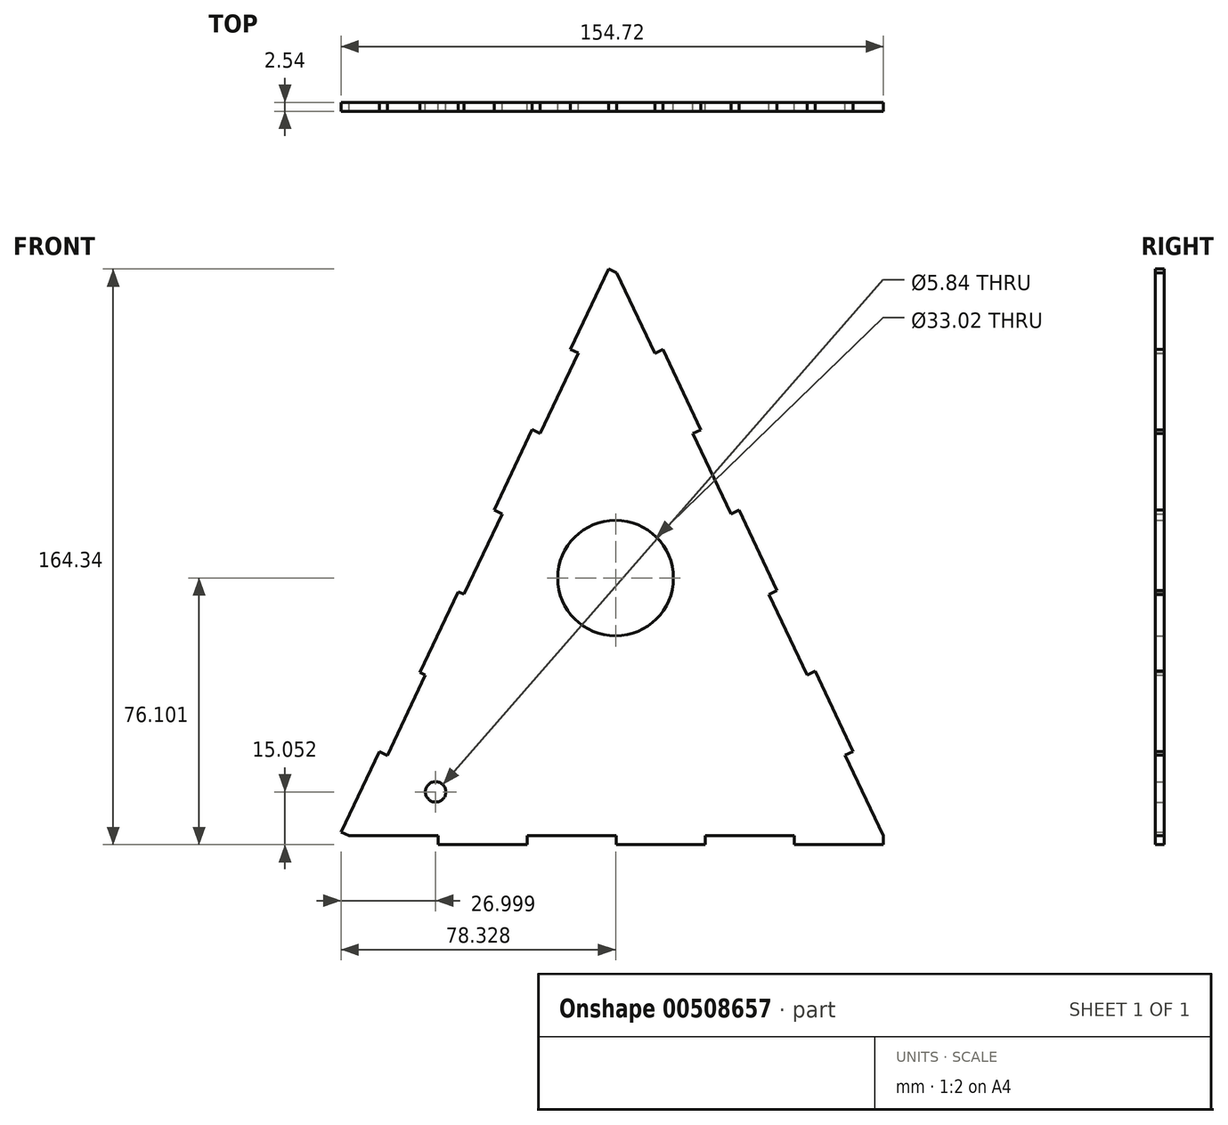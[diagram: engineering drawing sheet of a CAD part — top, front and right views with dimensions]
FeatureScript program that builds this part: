
annotation { "Feature Type Name" : "Feature", "Feature Type Description" : "" }
export const myFeature = defineFeature(function(context is Context, id is Id, definition is map)
    precondition{}
    {
        {
            var Q0;
            Q0=qCreatedBy(makeId("Front.planeOp"),FACE);
            var sketch = newSketch(context, id + "F0", { "sketchPlane" : qUnion([Q0])});
            skLineSegment(sketch, "E0", {"start": v(-10.9, 63.99) * mm, "end": v(-54.56, -27.9) * mm});
            skLineSegment(sketch, "E1", {"start": v(-76.36, -73.78) * mm, "end": v(76.06, -73.78) * mm});
            skLineSegment(sketch, "E2", {"start": v(76.06, -73.78) * mm, "end": v(0, 86.93) * mm});
            skLineSegment(sketch, "E3", {"start": v(0, 86.93) * mm, "end": v(-2.3, 88.02) * mm});
            skLineSegment(sketch, "E4", {"start": v(-2.3, 88.02) * mm, "end": v(-13.2, 65.08) * mm});
            skLineSegment(sketch, "E5", {"start": v(-13.2, 65.08) * mm, "end": v(-10.9, 63.99) * mm});
            skLineSegment(sketch, "E6", {"start": v(-24.1, 42.14) * mm, "end": v(-35, 19.2) * mm});
            skLineSegment(sketch, "E7", {"start": v(-35, 19.2) * mm, "end": v(-32.7, 18.1) * mm});
            skLineSegment(sketch, "E8", {"start": v(-43.6, -4.84) * mm, "end": v(-45.27, -4.19) * mm});
            skLineSegment(sketch, "E9", {"start": v(-45.27, -4.19) * mm, "end": v(-56.17, -27.13) * mm});
            skLineSegment(sketch, "E10", {"start": v(-56.17, -27.13) * mm, "end": v(-54.56, -27.9) * mm});
            skLineSegment(sketch, "E11", {"start": v(-54.56, -27.9) * mm, "end": v(-65.46, -50.84) * mm});
            skLineSegment(sketch, "E12", {"start": v(-65.46, -50.84) * mm, "end": v(-67.76, -49.75) * mm});
            skLineSegment(sketch, "E13", {"start": v(-67.76, -49.75) * mm, "end": v(-78.66, -72.7) * mm});
            skLineSegment(sketch, "E14", {"start": v(-78.66, -72.7) * mm, "end": v(-76.36, -73.78) * mm});
            skLineSegment(sketch, "E15", {"start": v(-76.36, -73.78) * mm, "end": v(-50.96, -73.78) * mm});
            skLineSegment(sketch, "E16", {"start": v(-50.96, -73.78) * mm, "end": v(-50.96, -76.32) * mm});
            skLineSegment(sketch, "E17", {"start": v(-50.96, -76.32) * mm, "end": v(-25.56, -76.32) * mm});
            skLineSegment(sketch, "E18", {"start": v(-25.56, -76.32) * mm, "end": v(-25.56, -73.78) * mm});
            skLineSegment(sketch, "E19", {"start": v(-25.56, -73.78) * mm, "end": v(-0.15, -73.78) * mm});
            skLineSegment(sketch, "E20", {"start": v(-0.15, -73.78) * mm, "end": v(-0.15, -76.32) * mm});
            skLineSegment(sketch, "E21", {"start": v(-0.15, -76.32) * mm, "end": v(25.25, -76.32) * mm});
            skLineSegment(sketch, "E22", {"start": v(25.25, -76.32) * mm, "end": v(25.25, -73.78) * mm});
            skLineSegment(sketch, "E23", {"start": v(25.25, -73.78) * mm, "end": v(50.65, -73.78) * mm});
            skLineSegment(sketch, "E24", {"start": v(50.65, -73.78) * mm, "end": v(50.65, -76.32) * mm});
            skLineSegment(sketch, "E25", {"start": v(50.65, -76.32) * mm, "end": v(76.05, -76.32) * mm});
            skLineSegment(sketch, "E26", {"start": v(76.05, -76.32) * mm, "end": v(76.06, -73.78) * mm});
            skLineSegment(sketch, "E27", {"start": v(76.06, -73.78) * mm, "end": v(65.2, -50.82) * mm});
            skLineSegment(sketch, "E28", {"start": v(65.2, -50.82) * mm, "end": v(67.5, -49.74) * mm});
            skLineSegment(sketch, "E29", {"start": v(67.5, -49.74) * mm, "end": v(56.62, -26.78) * mm});
            skLineSegment(sketch, "E30", {"start": v(56.62, -26.78) * mm, "end": v(54.33, -27.86) * mm});
            skLineSegment(sketch, "E31", {"start": v(43.46, -4.9) * mm, "end": v(45.76, -3.82) * mm});
            skLineSegment(sketch, "E32", {"start": v(45.76, -3.82) * mm, "end": v(34.9, 19.14) * mm});
            skLineSegment(sketch, "E33", {"start": v(34.9, 19.14) * mm, "end": v(32.6, 18.05) * mm});
            skLineSegment(sketch, "E34", {"start": v(21.73, 41.01) * mm, "end": v(24.03, 42.1) * mm});
            skLineSegment(sketch, "E35", {"start": v(24.03, 42.1) * mm, "end": v(13.16, 65.06) * mm});
            skLineSegment(sketch, "E36", {"start": v(13.16, 65.06) * mm, "end": v(10.87, 63.97) * mm});
            skLineSegment(sketch, "E37.trimOffspring", {"start": v(-65.46, -50.84) * mm, "end": v(-76.36, -73.78) * mm});
            skLineSegment(sketch, "E38", {"start": v(0, 86.93) * mm, "end": v(-10.9, 63.99) * mm});
            skLineSegment(sketch, "E39", {"start": v(-24.1, 42.14) * mm, "end": v(-21.8, 41.05) * mm});
            skCircle(sketch, "E40", {"center": v(-0.33, -0.22) * mm, "radius": 16.51 * mm});
            skCircle(sketch, "E41", {"center": v(-51.66, -61.27) * mm, "radius": 2.92 * mm});
            skSolve(sketch);
        }
        {
            var Q0;
            Q0=qSketchRegion(id+"F0",true);
            extrude(context, id + "F1", {"entities" : qUnion([Q0]), "depth" : 2.54 * mm, "offsetDistance" : 25.4 * mm});
        }
        {
            var Q0;
            Q0 = qSketchRegion(id + "F0", true);
            extrude(context, id + "F2", {"entities" : qUnion([Q0]), "operationType" : NewBodyOperationType.ADD, "depth" : 2.54 * mm, "offsetDistance" : 25.4 * mm});
        }
    });
